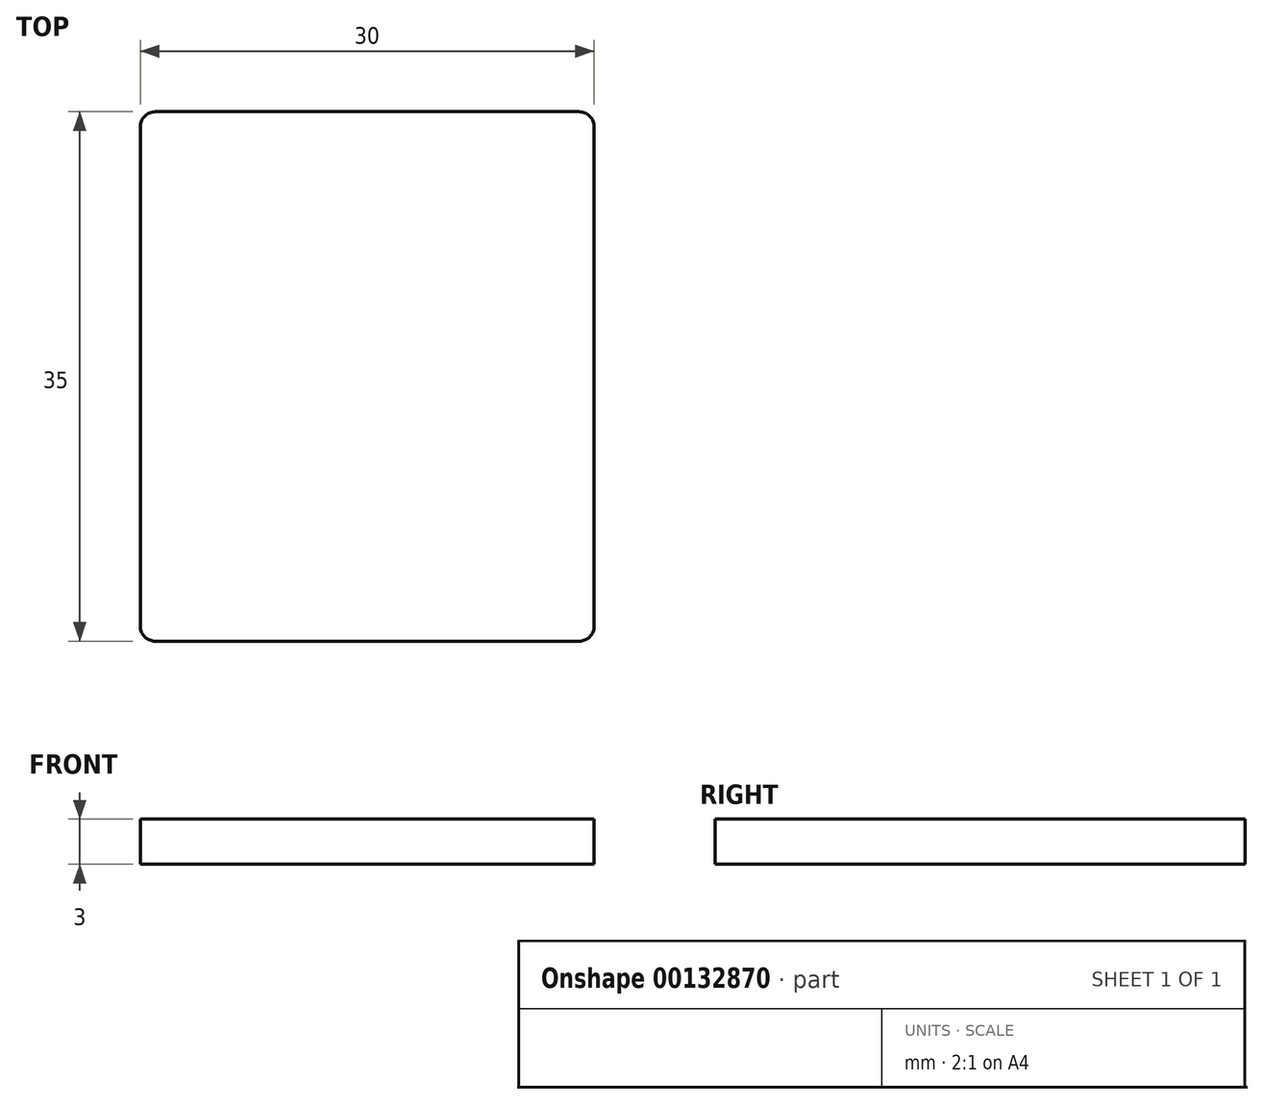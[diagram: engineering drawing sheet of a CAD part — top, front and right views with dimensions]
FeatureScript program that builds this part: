
annotation { "Feature Type Name" : "Feature", "Feature Type Description" : "" }
export const myFeature = defineFeature(function(context is Context, id is Id, definition is map)
    precondition{}
    {
        {
            var Q0;
            Q0=qCreatedBy(makeId("Top.planeOp"),FACE);
            var sketch = newSketch(context, id + "F0", { "sketchPlane" : qUnion([Q0])});
            skLineSegment(sketch, "E0.bottom", {"start": v(-15, 17.5) * mm, "end": v(15, 17.5) * mm});
            skLineSegment(sketch, "E0.top", {"start": v(-15, -17.5) * mm, "end": v(15, -17.5) * mm});
            skLineSegment(sketch, "E0.left", {"start": v(-15, 17.5) * mm, "end": v(-15, -17.5) * mm});
            skLineSegment(sketch, "E0.right", {"start": v(15, 17.5) * mm, "end": v(15, -17.5) * mm});
            skPoint(sketch, "E0.middle", {"position": v(0, 0) * mm});
            skSolve(sketch);
        }
        {
            var Q0;
            Q0 = qSketchRegion(id + "F0", true);
            extrude(context, id + "F1", {"entities" : qUnion([Q0]), "depth" : 3 * mm});
        }
        {
            var Q0;
            Q0=makeQuery(id+"F1.opExtrude","SWEPT_EDGE",EDGE,{"disambiguationData":[OSD([sQuery(id+"F0.wireOp",EDGE,"E0.top"),sQuery(id+"F0.wireOp",EDGE,"E0.left")])]});
            var Q1;
            Q1=makeQuery(id+"F1.opExtrude","SWEPT_EDGE",EDGE,{"disambiguationData":[OSD([sQuery(id+"F0.wireOp",EDGE,"E0.top"),sQuery(id+"F0.wireOp",EDGE,"E0.right")])]});
            var Q2;
            Q2=makeQuery(id+"F1.opExtrude","SWEPT_EDGE",EDGE,{"disambiguationData":[OSD([sQuery(id+"F0.wireOp",EDGE,"E0.bottom"),sQuery(id+"F0.wireOp",EDGE,"E0.right")])]});
            var Q3;
            Q3=makeQuery(id+"F1.opExtrude","SWEPT_EDGE",EDGE,{"disambiguationData":[OSD([sQuery(id+"F0.wireOp",EDGE,"E0.bottom"),sQuery(id+"F0.wireOp",EDGE,"E0.left")])]});
            fillet(context, id + "F2", {"entities" : qUnion([Q0, Q1, Q2, Q3]), "radius" : 1 * mm, "tangentPropagation" : true, "allowEdgeOverflow" : false});
        }
    });
